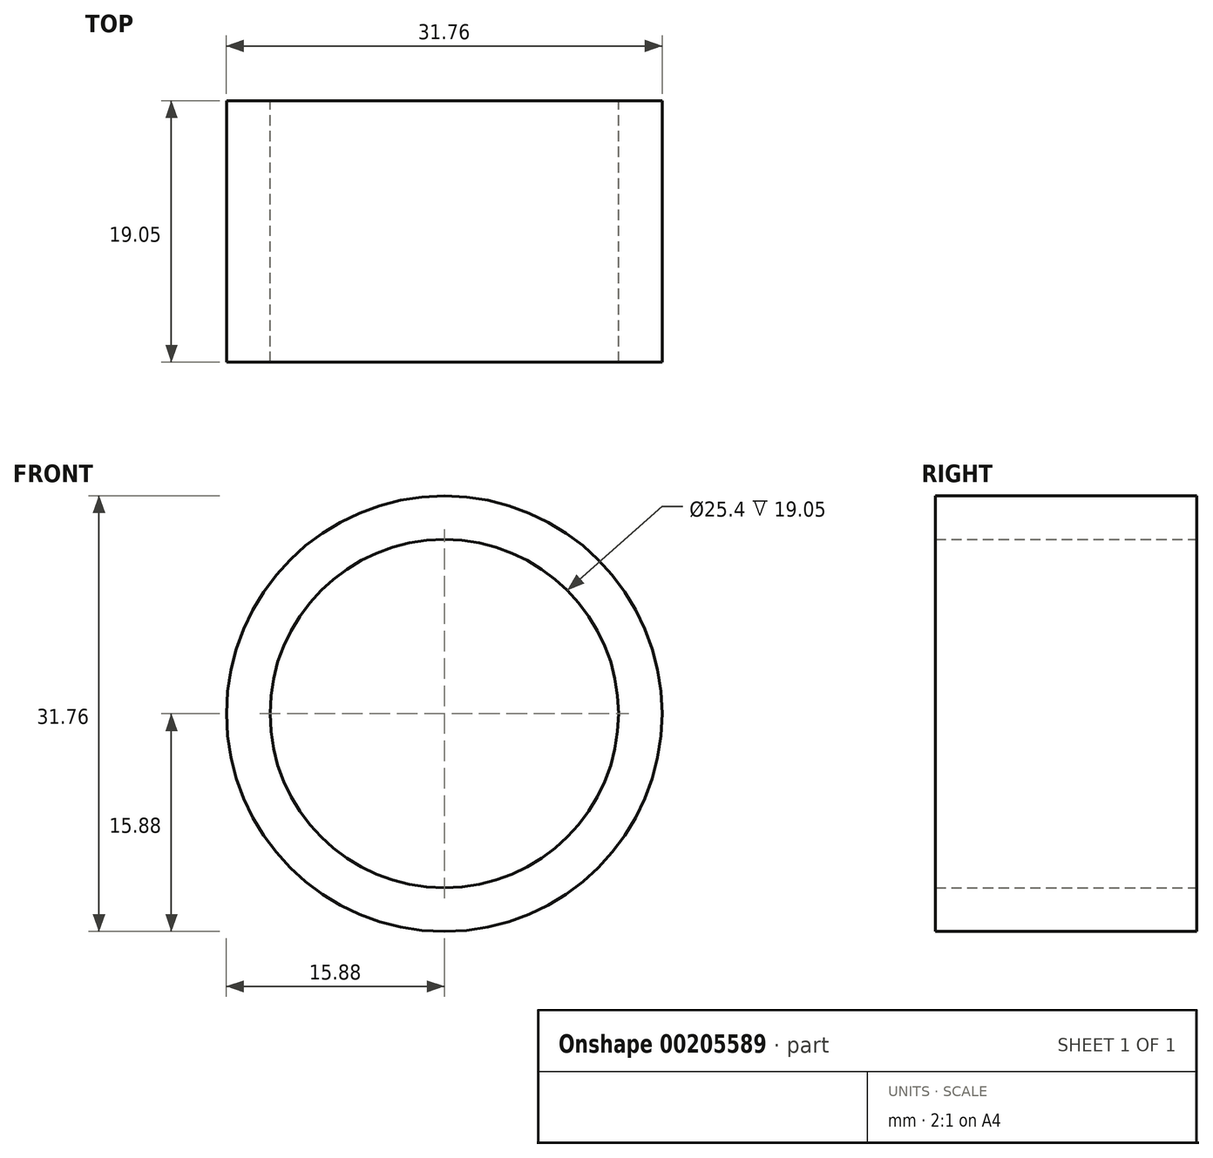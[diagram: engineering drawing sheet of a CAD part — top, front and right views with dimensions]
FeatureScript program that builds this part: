
annotation { "Feature Type Name" : "Feature", "Feature Type Description" : "" }
export const myFeature = defineFeature(function(context is Context, id is Id, definition is map)
    precondition{}
    {
        {
            var Q0;
            Q0=qCreatedBy(makeId("Front.planeOp"),FACE);
            var sketch = newSketch(context, id + "F0", { "sketchPlane" : qUnion([Q0])});
            skCircle(sketch, "E0", {"center": v(0, 0) * mm, "radius": 12.7 * mm});
            skCircle(sketch, "E1", {"center": v(0, 0) * mm, "radius": 15.88 * mm});
            skSolve(sketch);
        }
        {
            var Q0;
            Q0=qSketchRegion(id+"F0",true);
            extrude(context, id + "F1", {"entities" : qUnion([Q0]), "depth" : 19.05 * mm});
        }
    });
